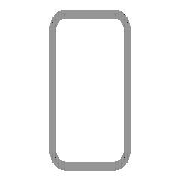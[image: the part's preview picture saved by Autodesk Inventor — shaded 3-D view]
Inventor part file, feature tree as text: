
AUTODESK INVENTOR PART (.ipt)
format: ipt  version: 2022 (Build 260153000, 153)  size: 215,552 bytes
history: native  units: mm (DEFAULTED — no unit token found)
features: other x5, sketch x3, plane x1
ambient origin geometry x8: Origin, YZ Plane, XZ Plane, XY Plane, X Axis, Y Axis, Z Axis, Center Point
bodies: Solid1 (feature_tree), Body (feature_tree), Solid6 (feature_tree)
feature tree (9):
  parser-record x1  (decoder bookkeeping rows leaked as tree rows — omitted from the tree; the rows remain in map.json)
  other  "Driven Length"
  other  "Start Plane"
  other  "End Plane"
  sketch  "Sketch"  dims[d7=7.5mm d10=50.0mm d11=30.0mm d12=5.0mm d13=-22.0mm d14=202.0mm d15=25.0mm d16=15.0mm d17=90.0deg d18=224.0mm]
  sketch  "Sketch3"  dims[d3=224.0mm]
  plane  "Work Plane3"
  sketch  "Sketch4"  dims[d4=0.0mm]
  other  "Srf5"
